# Revit family: Pilona Trajana FLEX P
name_source: partatom
category: Furniture
units: mm (PartAtom-declared; Revit-internal decimal feet)

## family parameters
Always vertical = Yes
Cut with Voids When Loaded = No
OmniClass Number = 23.40.20.00
OmniClass Title = General Furniture and Specialties
Room Calculation Point = No
Shared = No
Work Plane-Based = No

## types (1)
- Pilona Trajana FLEX P-H410P-130mm
    A = 0.13 m
    B = 0.1 m
    C = 0.073 m
    D = 0.18 m
    Default Elevation = 0 m
    Description = Pilona fabricada en polietileno de baja y alta densidad, compactado. Interior con goma reciclada de caucho
    Fabricante = BENITO URBAN SL
    Ficha Tecnica = https://www.benito.com
    H = 1 m
    H1 = 0.2 m
    Material = Polietilieno
    Referencia = H410P
    Type Comments = Con dos bandas reflectantes en la parte superior e inferior
    URL Producto = https://www.benito.com

## geometry (parser evidence)
native form markers: Blend x2, Sweep x2
no freeform markers — native parametric forms only
